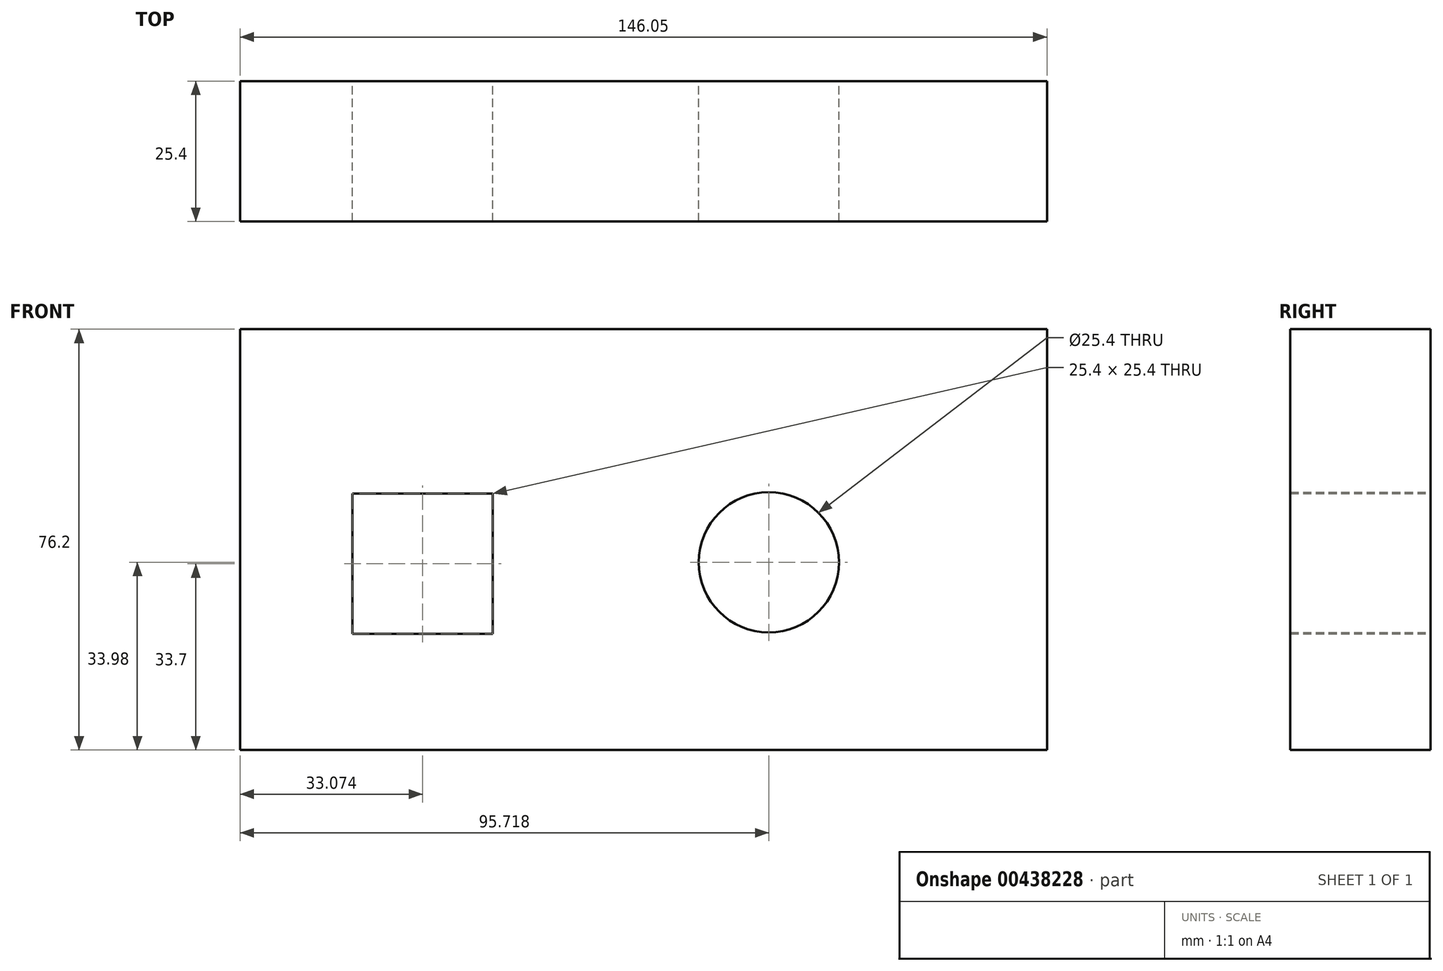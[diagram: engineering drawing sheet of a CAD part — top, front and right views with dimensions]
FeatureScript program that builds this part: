
annotation { "Feature Type Name" : "Feature", "Feature Type Description" : "" }
export const myFeature = defineFeature(function(context is Context, id is Id, definition is map)
    precondition{}
    {
        {
            var Q0;
            Q0=qCreatedBy(makeId("Front.planeOp"),FACE);
            var sketch = newSketch(context, id + "F0", { "sketchPlane" : qUnion([Q0])});
            skLineSegment(sketch, "E0.bottom", {"start": v(-65.64, 76.2) * mm, "end": v(80.4, 76.2) * mm});
            skLineSegment(sketch, "E0.top", {"start": v(-65.64, 0) * mm, "end": v(80.4, 0) * mm});
            skLineSegment(sketch, "E0.left", {"start": v(-65.64, 76.2) * mm, "end": v(-65.64, 0) * mm});
            skLineSegment(sketch, "E0.right", {"start": v(80.4, 76.2) * mm, "end": v(80.4, 0) * mm});
            skLineSegment(sketch, "E1.bottom", {"start": v(-45.27, 46.4) * mm, "end": v(-19.87, 46.4) * mm});
            skLineSegment(sketch, "E1.top", {"start": v(-45.27, 21) * mm, "end": v(-19.87, 21) * mm});
            skLineSegment(sketch, "E1.left", {"start": v(-45.27, 46.4) * mm, "end": v(-45.27, 21) * mm});
            skLineSegment(sketch, "E1.right", {"start": v(-19.87, 46.4) * mm, "end": v(-19.87, 21) * mm});
            skCircle(sketch, "E2", {"center": v(30.08, 33.98) * mm, "radius": 12.7 * mm});
            skSolve(sketch);
        }
        {
            var Q0;
            Q0=makeQuery(id+"F0.imprint","IMPRINT",FACE,{"disambiguationData":[TD([[makeQuery(id+"F0.imprint","IMPRINT",EDGE,{"derivedFrom":sQuery(id+"F0.wireOp",EDGE,"E0.bottom")}),-1.0]])]});
            extrude(context, id + "F1", {"entities" : qUnion([Q0]), "depth" : 25.4 * mm});
        }
    });
